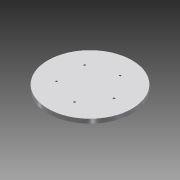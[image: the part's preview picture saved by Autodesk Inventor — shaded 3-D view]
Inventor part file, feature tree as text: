
AUTODESK INVENTOR PART (.ipt)
format: ipt  version: 2015 (Build 190159000, 159)  size: 261,120 bytes
history: native  units: in
note: dims shown in document units (in); Inventor stores cm internally (conversion verified against a paired STEP export)
features: sketch x8, extrude x7, fillet x1
ambient origin geometry x8: Origin, YZ Plane, XZ Plane, XY Plane, X Axis, Y Axis, Z Axis, Center Point
bodies: Solid1 (feature_tree)
feature tree (16):
  extrude  "Extrusion1"  Depth=0.2756in TaperAngle=0.0deg
  extrude  "Extrusion2"  Depth=0.1575in TaperAngle=0.0deg
  extrude  "Extrusion5"  Depth=0.9843in
  extrude  "Extrusion6"  Depth=0.0787in
  extrude  "Extrusion7"  Depth=0.0787in TaperAngle=0.0deg
  fillet  "Fillet1"  Radius=0.0787in
  sketch  "Sketch11"  dims[d48=0.9843in d49=0.0787in]
  extrude  "Extrusion9"  Depth=0.0787in
  extrude  "Extrusion10"  Depth=0.0787in
  sketch  "Sketch1"  dims[d0=5.5118in d1=0.2756in d2=0.0in]
  sketch  "Sketch2"  dims[d3=0.315in d4=0.1575in d5=0.0in]
  sketch  "Sketch7"  dims[d35=0.9843in d36=1.5354in]
  sketch  "Sketch8"  dims[d37=0.7087in d38=0.0787in]
  sketch  "Sketch9"  dims[d39=1.9685in d41=360.0deg d43=0.0787in d44=0.0in d46=0.0787in d47=0.0in]
  sketch  "Sketch13"  dims[d50=0.1181in d51=0.0787in]
  sketch  "Sketch14"  dims[d52=0.0591in d53=0.0in d54=0.0591in d58=0.0344in d65=0.1181in d66=1.5748in d67=0.1575in d68=0.0in d69=1.9685in d71=360.0deg d73=0.315in d74=0.5906in d75=0.0in]
